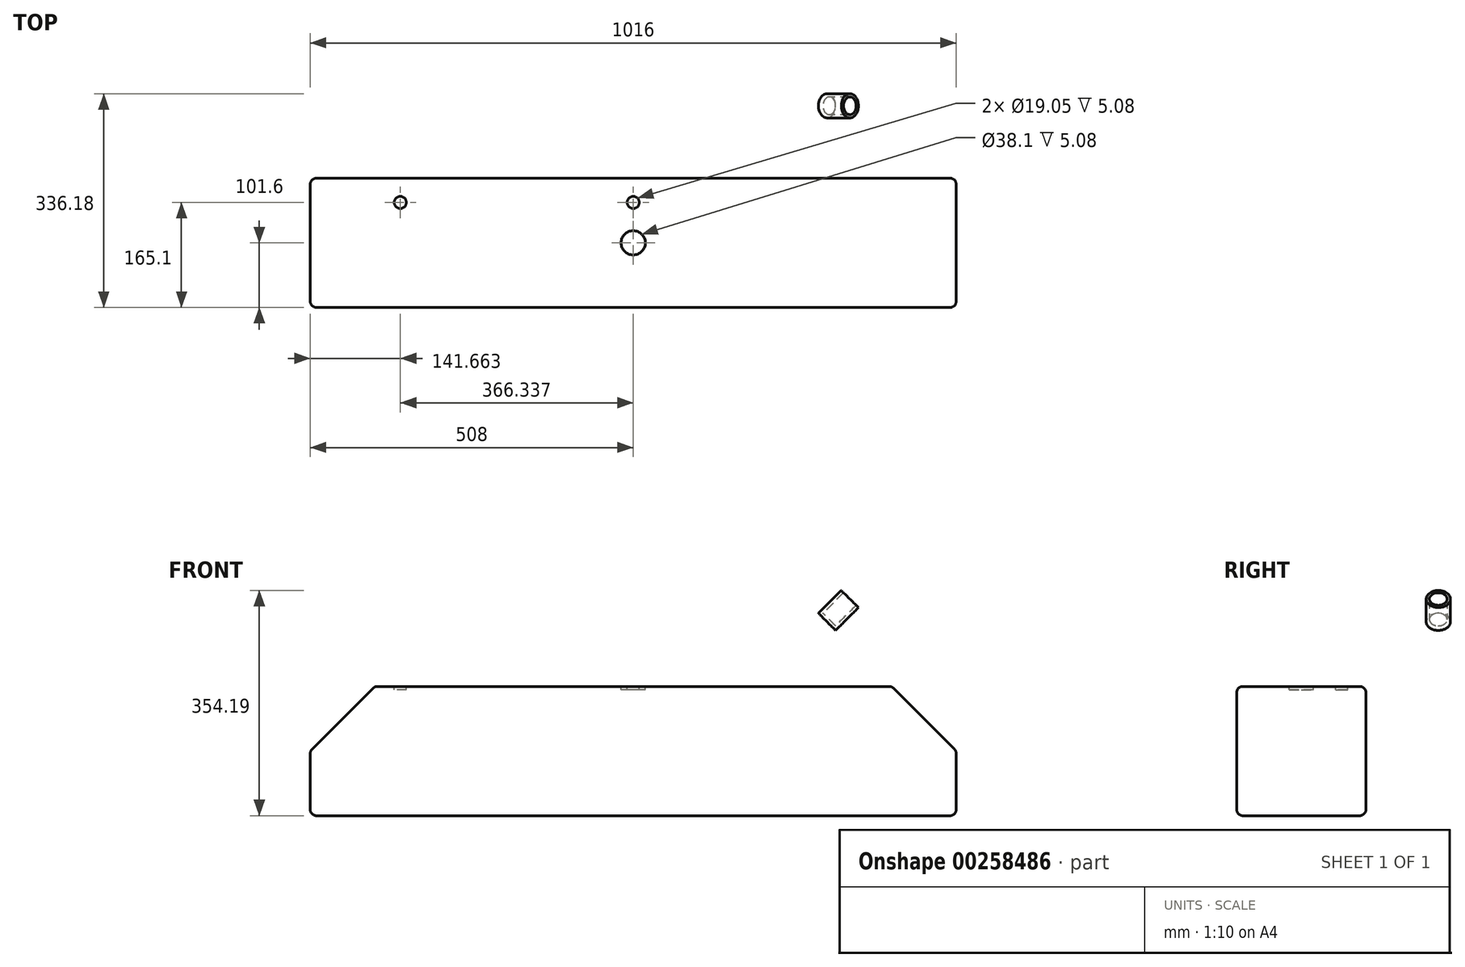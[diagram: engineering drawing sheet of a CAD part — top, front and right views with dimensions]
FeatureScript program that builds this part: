
annotation { "Feature Type Name" : "Feature", "Feature Type Description" : "" }
export const myFeature = defineFeature(function(context is Context, id is Id, definition is map)
    precondition{}
    {
        {
            var Q0;
            Q0=qCreatedBy(makeId("Top.planeOp"),FACE);
            var sketch = newSketch(context, id + "F0", { "sketchPlane" : qUnion([Q0])});
            skLineSegment(sketch, "E0.bottom", {"start": v(508, 101.6) * mm, "end": v(-508, 101.6) * mm});
            skLineSegment(sketch, "E0.top", {"start": v(508, -101.6) * mm, "end": v(-508, -101.6) * mm});
            skLineSegment(sketch, "E0.left", {"start": v(508, 101.6) * mm, "end": v(508, -101.6) * mm});
            skLineSegment(sketch, "E0.right", {"start": v(-508, 101.6) * mm, "end": v(-508, -101.6) * mm});
            skPoint(sketch, "E0.middle", {"position": v(0, 0) * mm});
            skSolve(sketch);
        }
        {
            var Q0;
            Q0=makeQuery(id+"F0.imprint","IMPRINT",FACE,{"disambiguationData":[TD([[makeQuery(id+"F0.imprint","IMPRINT",EDGE,{"derivedFrom":sQuery(id+"F0.wireOp",EDGE,"E0.bottom")}),1.0]])]});
            extrude(context, id + "F1", {"entities" : qUnion([Q0]), "depth" : 203.2 * mm});
        }
        {
            var Q0;
            Q0=makeQuery(id+"F1.opExtrude","SWEPT_FACE",FACE,{"disambiguationData":[OSD([sQuery(id+"F0.wireOp",EDGE,"E0.top")])]});
            var sketch = newSketch(context, id + "F2", { "sketchPlane" : qUnion([Q0])});
            skLineSegment(sketch, "E1", {"start": v(0, 0) * mm, "end": v(0, 203.2) * mm, "construction": true});
            skLineSegment(sketch, "E2", {"start": v(-508, 101.6) * mm, "end": v(-406.4, 203.2) * mm});
            skLineSegment(sketch, "E3.MirrorCS", {"start": v(508, 101.6) * mm, "end": v(406.4, 203.2) * mm});
            skSolve(sketch);
        }
        {
            var Q0;
            {var subQ0=sQuery(id+"F2.wireOp",EDGE,"E2");Q0=makeQuery(id+"F2.imprint","IMPRINT",FACE,{"disambiguationData":[TD([[makeQuery(id+"F2.imprint","IMPRINT",EDGE,{"derivedFrom":subQ0}),1.0]])]});}
            var Q1;
            {var subQ0=sQuery(id+"F2.wireOp",EDGE,"E3.MirrorCS");Q1=makeQuery(id+"F2.imprint","IMPRINT",FACE,{"disambiguationData":[TD([[makeQuery(id+"F2.imprint","IMPRINT",EDGE,{"derivedFrom":subQ0}),-1.0]])]});}
            extrude(context, id + "F3", {"entities" : qUnion([Q0, Q1]), "operationType" : NewBodyOperationType.REMOVE, "endBound" : BoundingType.THROUGH_ALL, "oppositeDirection" : true, "depth" : 25.4 * mm});
        }
        {
            var Q0;
            Q0=makeQuery(id+"F3.boolean.opBoolean","COPY",FACE,{"derivedFrom":makeQuery(id+"F3.opExtrude","SWEPT_FACE",FACE,{"disambiguationData":[OSD([sQuery(id+"F2.wireOp",EDGE,"E3.MirrorCS")])]})});
            var sketch = newSketch(context, id + "F4", { "sketchPlane" : qUnion([Q0])});
            skCircle(sketch, "E4", {"center": v(215.53, 0) * mm, "radius": 19.05 * mm});
            skPoint(sketch, "E4.centerSnap0", {"position": v(215.53, -101.6) * mm});
            skSolve(sketch);
        }
        {
            var Q0;
            Q0=makeQuery(id+"F4.imprint","IMPRINT",FACE,{"disambiguationData":[TD([[makeQuery(id+"F4.imprint","IMPRINT",EDGE,{"derivedFrom":sQuery(id+"F4.wireOp",EDGE,"E4")}),1.0]])]});
            extrude(context, id + "F5", {"entities" : qUnion([Q0]), "operationType" : NewBodyOperationType.ADD, "depth" : 50.8 * mm});
        }
        {
            var Q0;
            Q0=makeQuery(id+"F1.opExtrude","SWEPT_FACE",FACE,{"disambiguationData":[OSD([sQuery(id+"F0.wireOp",EDGE,"E0.top")])]});
            var Q1;
            Q1=makeQuery(id+"F3.boolean.opBoolean","COPY",FACE,{"derivedFrom":makeQuery(id+"F3.opExtrude","SWEPT_FACE",FACE,{"disambiguationData":[OSD([sQuery(id+"F2.wireOp",EDGE,"E3.MirrorCS")])]})});
            var Q2;
            Q2=makeQuery(id+"F1.opExtrude","SWEPT_FACE",FACE,{"disambiguationData":[OSD([sQuery(id+"F0.wireOp",EDGE,"E0.left")])]});
            var Q3;
            Q3=makeQuery(id+"F1.opExtrude","CAP_FACE",FACE,{"disambiguationData":[OSD([sQuery(id+"F0.wireOp",EDGE,"E0.bottom"),sQuery(id+"F0.wireOp",EDGE,"E0.top"),sQuery(id+"F0.wireOp",EDGE,"E0.left"),sQuery(id+"F0.wireOp",EDGE,"E0.right")])],"isStart":false});
            var Q4;
            Q4=makeQuery(id+"F1.opExtrude","SWEPT_FACE",FACE,{"disambiguationData":[OSD([sQuery(id+"F0.wireOp",EDGE,"E0.right")])]});
            var Q5;
            Q5=makeQuery(id+"F3.boolean.opBoolean","COPY",FACE,{"derivedFrom":makeQuery(id+"F3.opExtrude","SWEPT_FACE",FACE,{"disambiguationData":[OSD([sQuery(id+"F2.wireOp",EDGE,"E2")])]})});
            var Q6;
            Q6=makeQuery(id+"F1.opExtrude","SWEPT_FACE",FACE,{"disambiguationData":[OSD([sQuery(id+"F0.wireOp",EDGE,"E0.bottom")])]});
            fillet(context, id + "F6", {"entities" : qUnion([Q0, Q1, Q2, Q3, Q4, Q5, Q6]), "radius" : 9.52 * mm, "tangentPropagation" : true, "allowEdgeOverflow" : false});
        }
        {
            var Q0;
            Q0=makeQuery(id+"F5.opExtrude","CAP_FACE",FACE,{"disambiguationData":[OSD([sQuery(id+"F4.wireOp",EDGE,"E4")])],"isStart":false});
            shell(context, id + "F7", {"entities" : qUnion([Q0]), "thickness" : 5.08 * mm});
        }
        {
            var Q0;
            Q0=makeQuery(id+"F1.opExtrude","CAP_FACE",FACE,{"disambiguationData":[OSD([sQuery(id+"F0.wireOp",EDGE,"E0.bottom"),sQuery(id+"F0.wireOp",EDGE,"E0.top"),sQuery(id+"F0.wireOp",EDGE,"E0.left"),sQuery(id+"F0.wireOp",EDGE,"E0.right")])],"isStart":false});
            var sketch = newSketch(context, id + "F8", { "sketchPlane" : qUnion([Q0])});
            skCircle(sketch, "E5", {"center": v(0, 0) * mm, "radius": 19.05 * mm});
            skCircle(sketch, "E6", {"center": v(-366.34, 63.5) * mm, "radius": 9.53 * mm});
            skCircle(sketch, "E7", {"center": v(0, 63.5) * mm, "radius": 9.53 * mm});
            skSolve(sketch);
        }
        {
            var Q0;
            Q0=makeQuery(id+"F8.imprint","IMPRINT",FACE,{"disambiguationData":[TD([[makeQuery(id+"F8.imprint","IMPRINT",EDGE,{"derivedFrom":sQuery(id+"F8.wireOp",EDGE,"E6")}),1.0]])]});
            var Q1;
            Q1=makeQuery(id+"F8.imprint","IMPRINT",FACE,{"disambiguationData":[TD([[makeQuery(id+"F8.imprint","IMPRINT",EDGE,{"derivedFrom":sQuery(id+"F8.wireOp",EDGE,"E7")}),1.0]])]});
            var Q2;
            Q2=makeQuery(id+"F8.imprint","IMPRINT",FACE,{"disambiguationData":[TD([[makeQuery(id+"F8.imprint","IMPRINT",EDGE,{"derivedFrom":sQuery(id+"F8.wireOp",EDGE,"E5")}),1.0]])]});
            extrude(context, id + "F9", {"entities" : qUnion([Q0, Q1, Q2]), "operationType" : NewBodyOperationType.REMOVE, "oppositeDirection" : true, "depth" : 5.08 * mm});
        }
    });
